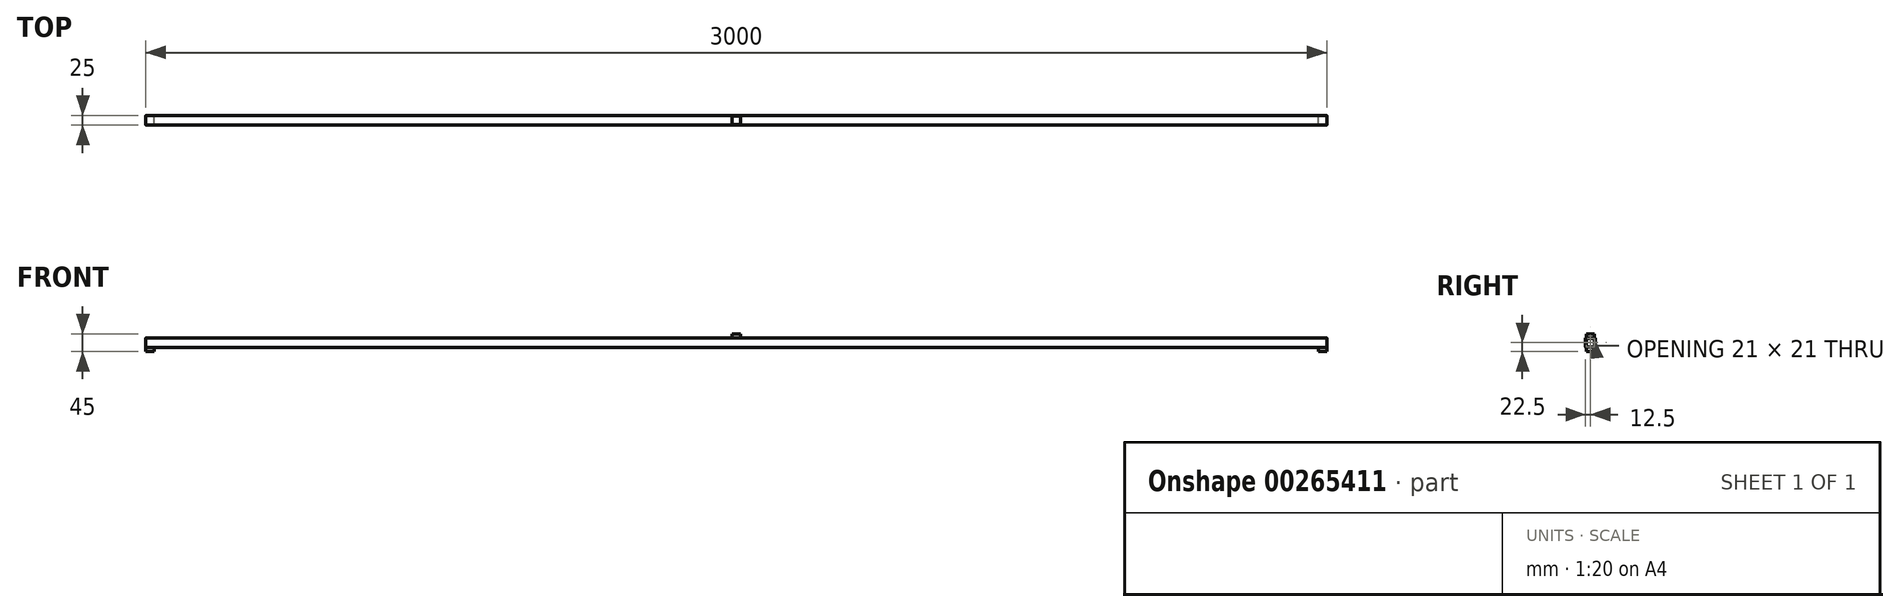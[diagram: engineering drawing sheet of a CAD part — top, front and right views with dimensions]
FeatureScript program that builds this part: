
annotation { "Feature Type Name" : "Feature", "Feature Type Description" : "" }
export const myFeature = defineFeature(function(context is Context, id is Id, definition is map)
    precondition{}
    {
        {
            var Q0;
            Q0=qCreatedBy(makeId("Right.planeOp"),FACE);
            var sketch = newSketch(context, id + "F0", { "sketchPlane" : qUnion([Q0])});
            skLineSegment(sketch, "E0.bottom", {"start": v(10.5, 12.5) * mm, "end": v(-10.5, 12.5) * mm});
            skLineSegment(sketch, "E0.top", {"start": v(10.5, -12.5) * mm, "end": v(-10.5, -12.5) * mm});
            skLineSegment(sketch, "E0.left", {"start": v(12.5, 10.5) * mm, "end": v(12.5, -10.5) * mm});
            skLineSegment(sketch, "E0.right", {"start": v(-12.5, 10.5) * mm, "end": v(-12.5, -10.5) * mm});
            skPoint(sketch, "E0.middle", {"position": v(0, 0) * mm});
            skLineSegment(sketch, "E1.bottom", {"start": v(8.5, 10.5) * mm, "end": v(-8.5, 10.5) * mm});
            skLineSegment(sketch, "E1.top", {"start": v(8.5, -10.5) * mm, "end": v(-8.5, -10.5) * mm});
            skLineSegment(sketch, "E1.left", {"start": v(10.5, 8.5) * mm, "end": v(10.5, -8.5) * mm});
            skLineSegment(sketch, "E1.right", {"start": v(-10.5, 8.5) * mm, "end": v(-10.5, -8.5) * mm});
            skPoint(sketch, "E2.visualSharp", {"position": v(-12.5, 12.5) * mm});
            skArc(sketch, "E2.filletArc", {"start": v(-10.5, 12.5) * mm, "mid": v(-11.91, 11.91) * mm, "end": v(-12.5, 10.5) * mm});
            skPoint(sketch, "E3.visualSharp", {"position": v(12.5, 12.5) * mm});
            skArc(sketch, "E3.filletArc", {"start": v(12.5, 10.5) * mm, "mid": v(11.91, 11.91) * mm, "end": v(10.5, 12.5) * mm});
            skPoint(sketch, "E4.visualSharp", {"position": v(12.5, -12.5) * mm});
            skArc(sketch, "E4.filletArc", {"start": v(10.5, -12.5) * mm, "mid": v(11.91, -11.91) * mm, "end": v(12.5, -10.5) * mm});
            skPoint(sketch, "E5.visualSharp", {"position": v(-12.5, -12.5) * mm});
            skArc(sketch, "E5.filletArc", {"start": v(-12.5, -10.5) * mm, "mid": v(-11.91, -11.91) * mm, "end": v(-10.5, -12.5) * mm});
            skArc(sketch, "E6.filletArc", {"start": v(-10.5, -8.5) * mm, "mid": v(-9.91, -9.91) * mm, "end": v(-8.5, -10.5) * mm});
            skArc(sketch, "E7.filletArc", {"start": v(8.5, -10.5) * mm, "mid": v(9.91, -9.91) * mm, "end": v(10.5, -8.5) * mm});
            skArc(sketch, "E8.filletArc", {"start": v(10.5, 8.5) * mm, "mid": v(9.91, 9.91) * mm, "end": v(8.5, 10.5) * mm});
            skArc(sketch, "E9.filletArc", {"start": v(-8.5, 10.5) * mm, "mid": v(-9.91, 9.91) * mm, "end": v(-10.5, 8.5) * mm});
            skSolve(sketch);
        }
        {
            var Q0;
            Q0=makeQuery(id+"F0.imprint","IMPRINT",FACE,{"disambiguationData":[TD([[makeQuery(id+"F0.imprint","IMPRINT",EDGE,{"derivedFrom":sQuery(id+"F0.wireOp",EDGE,"E0.bottom")}),1.0]])]});
            extrude(context, id + "F1", {"entities" : qUnion([Q0]), "endBound" : BoundingType.SYMMETRIC, "depth" : 3000 * mm});
        }
        {
            var Q0;
            Q0=makeQuery(id+"F1.opExtrude","SWEPT_FACE",FACE,{"disambiguationData":[OSD([sQuery(id+"F0.wireOp",EDGE,"E0.top")])]});
            var sketch = newSketch(context, id + "F2", { "sketchPlane" : qUnion([Q0])});
            skLineSegment(sketch, "E10.bottom", {"start": v(1500, 10.5) * mm, "end": v(1479, 10.5) * mm});
            skLineSegment(sketch, "E10.top", {"start": v(1500, -10.5) * mm, "end": v(1479, -10.5) * mm});
            skLineSegment(sketch, "E10.left", {"start": v(1500, 10.5) * mm, "end": v(1500, -10.5) * mm});
            skLineSegment(sketch, "E10.right", {"start": v(1479, 10.5) * mm, "end": v(1479, -10.5) * mm});
            skLineSegment(sketch, "E11.bottom", {"start": v(-1500, 10.5) * mm, "end": v(-1478.88, 10.5) * mm});
            skLineSegment(sketch, "E11.top", {"start": v(-1500, -10.5) * mm, "end": v(-1478.88, -10.5) * mm});
            skLineSegment(sketch, "E11.left", {"start": v(-1500, 10.5) * mm, "end": v(-1500, -10.5) * mm});
            skLineSegment(sketch, "E11.right", {"start": v(-1478.88, 10.5) * mm, "end": v(-1478.88, -10.5) * mm});
            skSolve(sketch);
        }
        {
            var Q0;
            Q0=makeQuery(id+"F2.imprint","IMPRINT",FACE,{"disambiguationData":[TD([[makeQuery(id+"F2.imprint","IMPRINT",EDGE,{"derivedFrom":sQuery(id+"F2.wireOp",EDGE,"E11.bottom")}),1.0]])]});
            extrude(context, id + "F3", {"entities" : qUnion([Q0]), "operationType" : NewBodyOperationType.ADD, "depth" : 10 * mm});
        }
        {
            var Q0;
            Q0 = qSketchRegion(id + "F2", true);
            extrude(context, id + "F4", {"entities" : qUnion([Q0]), "operationType" : NewBodyOperationType.ADD, "depth" : 10 * mm});
        }
        {
            var Q0;
            Q0=makeQuery(id+"F1.opExtrude","SWEPT_FACE",FACE,{"disambiguationData":[OSD([sQuery(id+"F0.wireOp",EDGE,"E0.bottom")])]});
            var sketch = newSketch(context, id + "F5", { "sketchPlane" : qUnion([Q0])});
            skLineSegment(sketch, "E12.bottom", {"start": v(10.3, 10.5) * mm, "end": v(-10.3, 10.5) * mm});
            skLineSegment(sketch, "E12.top", {"start": v(10.3, -10.5) * mm, "end": v(-10.3, -10.5) * mm});
            skLineSegment(sketch, "E12.left", {"start": v(10.3, 10.5) * mm, "end": v(10.3, -10.5) * mm});
            skLineSegment(sketch, "E12.right", {"start": v(-10.3, 10.5) * mm, "end": v(-10.3, -10.5) * mm});
            skPoint(sketch, "E12.middle", {"position": v(0, 0) * mm});
            skSolve(sketch);
        }
        {
            var Q0;
            Q0=makeQuery(id+"F5.imprint","IMPRINT",FACE,{"disambiguationData":[TD([[makeQuery(id+"F5.imprint","IMPRINT",EDGE,{"derivedFrom":sQuery(id+"F5.wireOp",EDGE,"E12.bottom")}),1.0]])]});
            extrude(context, id + "F6", {"entities" : qUnion([Q0]), "operationType" : NewBodyOperationType.ADD, "depth" : 10 * mm});
        }
    });
